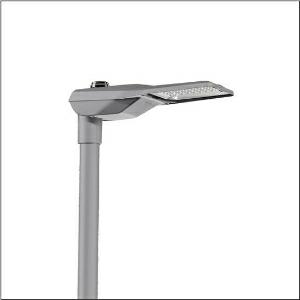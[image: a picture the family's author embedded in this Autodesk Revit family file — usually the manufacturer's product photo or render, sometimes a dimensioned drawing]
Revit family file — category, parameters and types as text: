
# Revit family: streetlight_sl_21_mini___st1_0a_5xe6d37n08gb_0daf
name_source: partatom
category: Lighting Fixtures
units: mm (PartAtom-declared; Revit-internal decimal feet)

## family parameters
Cut with Voids When Loaded = No
Host = Face
Light Source = No
Part Type = Normal
Room Calculation Point = No
Round Connector Dimension = Use Diameter
Shared = No

## types (1)
- --- (1 x LED, 5940 lm, 40.4 W, 3000K)
    Apparent Load = 40 VA
    CIE Flux Codes = 37 72 97 100 100
    Color Rendering = 70
    Color Temperature = 3000K
    Default Elevation = 1800 mm
    Description = Streetlight SL 21 mini, mast luminaire, primary light control with lens, of PMMA, primary optical cover: cover, of toughened safety glass, transparent, light distribution: ST1.0a, light emission: direct distribution, primary light characteristic: asymmetric, installation type: side-entry, LED, 3G 1.5mm², High Power LED, rated luminous flux: 5.940lm, luminous efficacy: 147lm/W, light colour: 730, colour temperature: 3000K, control gear: NEMA (7pin), control: overheat protection, pre-setting: linear dimming characteristic, constant luminous flux control, time-dependent luminous flux control, flexible luminous flux parameterisation, mains connection: 230..240V, AC, 50/60Hz, connection cable pre-assembled, cable length: 8,5m, wiring characteristics: H07RN-F, start of lifetime: 40W, end of service life: 41W, reduction: 19W, luminaire housing, of diecast aluminium (EN AC-44300), powder-coated, SITECO metallic grey (DB 702S), corrosivity category C5 high according to DIN EN ISO 12944, multi-level sealing system, sealing non-destructively replaceable, inclination adjustable: 0°, 5°, 10°, 15°, length: 628mm, width: 235mm, height: 110mm, spigot size: 42mm (side-entry), mounting height: 4..8m, protection rating (complete): IP66, insulation class (complete): insulation class I (protective earthing), certification: CE, ENEC, ENEC+, VDE, impact resistance: IK10, permissible operating ambient temperature for outdoor applications: -40..+50°C, standard-compliant lighting for roads and squares, packaging unit: 1 piece

Light Distribution: ST1.0a
    Height = 110 mm
    Lamp = 1 x LED
    Lamp Light Flux = 5940 lm
    Lamp Power = 40.4 W
    Lamp count = 1
    Length = 625 mm
    Luminous efficacy = 147 lm/W
    Manufacturer = Siteco
    ModVariant = No
    Model = 5XE6D37N08GB
    Number of Poles = 1
    OnlyDefault = Yes
    Power Factor = 1
    Product Name = Streetlight SL 21 mini | ST1.0a
    Product group = mast luminaire | pylon top
    ProductGroupID = 6100
    Protection Class = Protection class I
    Protection Degree = IP 66
    RLX_Detail_Level = 1
    RLX_Emergency_Light_Flux = 0 lm
    RLX_Emergency_Type = 0
    RLX_Emergency_Type_DB = No
    RlxData = <blob elided: 25805 chars, md5=51707b1c>
    Socket = socket
    Standby Power = 0 W
    System Light Flux = 5940 lm
    System Power = 40 W
    Type Comments = factory setting: luminous flux: 100 % | dim-lin: 254 | 812 mA
    Type Image = l_1294379.jpg
    URL = http://relux.com
    VarID = @adj_135817
    Voltage = 0 V
    Weight = 0.00 kg
    Width = 234 mm

## geometry (parser evidence)
native form markers: Blend x4, Sweep x10
no freeform markers — native parametric forms only
